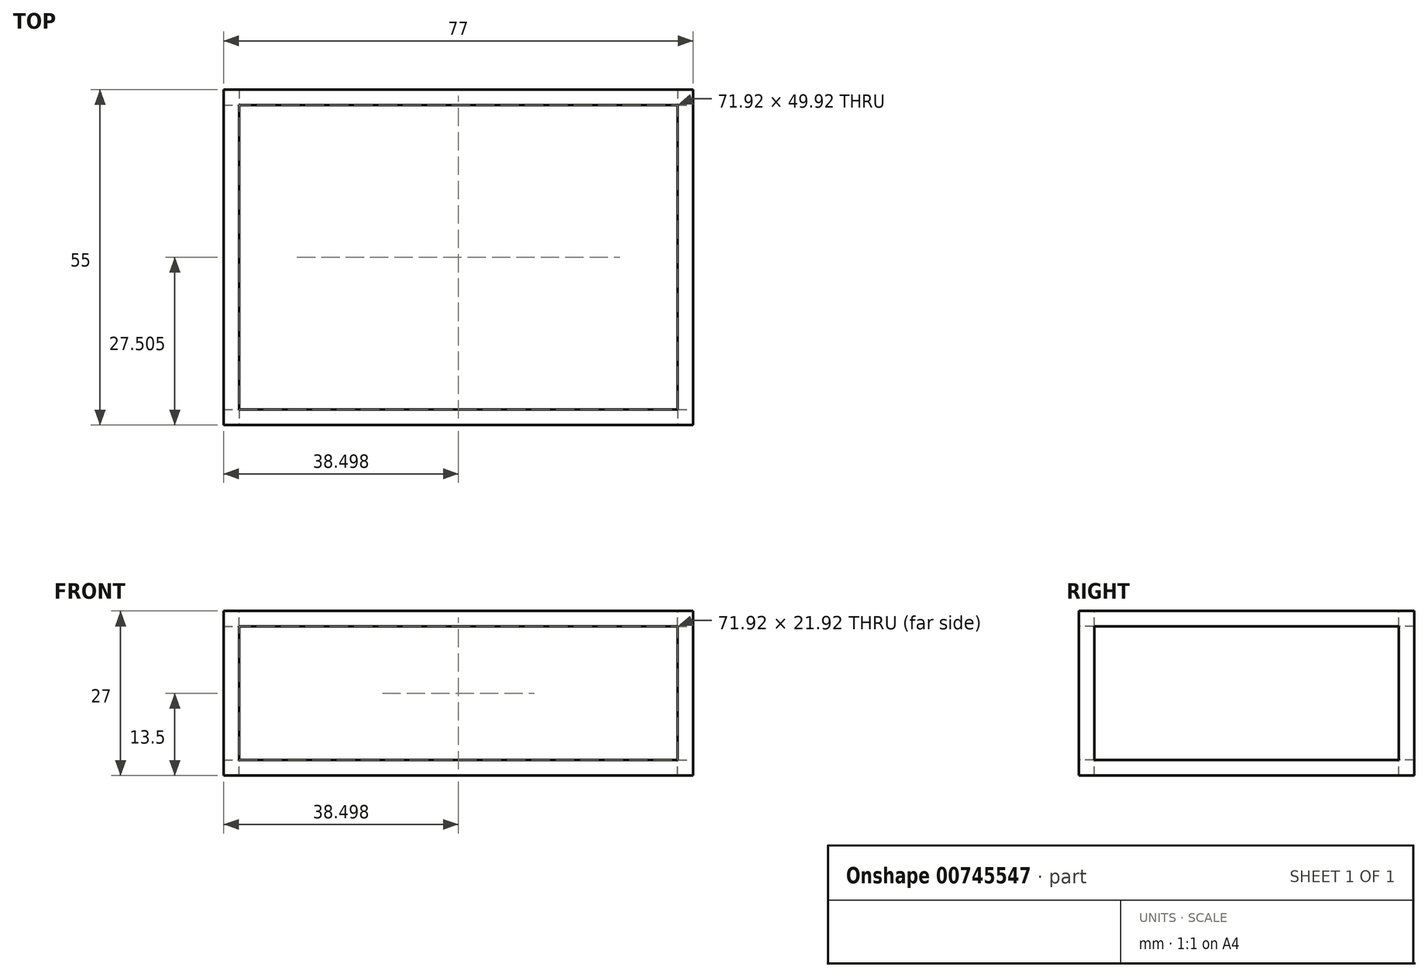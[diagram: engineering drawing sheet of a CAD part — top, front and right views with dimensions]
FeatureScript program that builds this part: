
annotation { "Feature Type Name" : "Feature", "Feature Type Description" : "" }
export const myFeature = defineFeature(function(context is Context, id is Id, definition is map)
    precondition{}
    {
        {
            var Q0;
            Q0=qCreatedBy(makeId("Top.planeOp"),FACE);
            var sketch = newSketch(context, id + "F0", { "sketchPlane" : qUnion([Q0])});
            skLineSegment(sketch, "E0.bottom", {"start": v(-34.82, 42.65) * mm, "end": v(42.18, 42.65) * mm});
            skLineSegment(sketch, "E0.top", {"start": v(-34.82, -12.35) * mm, "end": v(42.18, -12.35) * mm});
            skLineSegment(sketch, "E0.left", {"start": v(-34.82, 42.65) * mm, "end": v(-34.82, -12.35) * mm});
            skLineSegment(sketch, "E0.right", {"start": v(42.18, 42.65) * mm, "end": v(42.18, -12.35) * mm});
            skSolve(sketch);
        }
        {
            var Q0;
            Q0=makeQuery(id+"F0.imprint","IMPRINT",FACE,{"disambiguationData":[TD([[makeQuery(id+"F0.imprint","IMPRINT",EDGE,{"derivedFrom":sQuery(id+"F0.wireOp",EDGE,"E0.bottom")}),-1.0]])]});
            extrude(context, id + "F1", {"entities" : qUnion([Q0]), "depth" : 27 * mm, "offsetDistance" : 25.4 * mm});
        }
        {
            var Q0;
            Q0=makeQuery(id+"F1.opExtrude","CAP_FACE",FACE,{"disambiguationData":[OSD([sQuery(id+"F0.wireOp",EDGE,"E0.bottom"),sQuery(id+"F0.wireOp",EDGE,"E0.top"),sQuery(id+"F0.wireOp",EDGE,"E0.left"),sQuery(id+"F0.wireOp",EDGE,"E0.right")])],"isStart":false});
            var sketch = newSketch(context, id + "F2", { "sketchPlane" : qUnion([Q0])});
            skLineSegment(sketch, "E1.bottom", {"start": v(-32.28, 40.11) * mm, "end": v(39.64, 40.11) * mm});
            skLineSegment(sketch, "E1.top", {"start": v(-32.28, -9.8) * mm, "end": v(39.64, -9.8) * mm});
            skLineSegment(sketch, "E1.left", {"start": v(-32.28, 40.11) * mm, "end": v(-32.28, -9.8) * mm});
            skLineSegment(sketch, "E1.right", {"start": v(39.64, 40.11) * mm, "end": v(39.64, -9.8) * mm});
            skSolve(sketch);
        }
        {
            var Q0;
            Q0=makeQuery(id+"F2.imprint","IMPRINT",FACE,{"disambiguationData":[TD([[makeQuery(id+"F2.imprint","IMPRINT",EDGE,{"derivedFrom":sQuery(id+"F2.wireOp",EDGE,"E1.bottom")}),-1.0]])]});
            extrude(context, id + "F3", {"entities" : qUnion([Q0]), "operationType" : NewBodyOperationType.REMOVE, "oppositeDirection" : true, "depth" : 27 * mm, "offsetDistance" : 25.4 * mm});
        }
        {
            var Q0;
            Q0=makeQuery(id+"F1.opExtrude","SWEPT_FACE",FACE,{"disambiguationData":[OSD([sQuery(id+"F0.wireOp",EDGE,"E0.right")])]});
            var sketch = newSketch(context, id + "F4", { "sketchPlane" : qUnion([Q0])});
            skLineSegment(sketch, "E2.bottom", {"start": v(40.11, 24.46) * mm, "end": v(-9.8, 24.46) * mm});
            skLineSegment(sketch, "E2.top", {"start": v(40.11, 2.54) * mm, "end": v(-9.8, 2.54) * mm});
            skLineSegment(sketch, "E2.left", {"start": v(40.11, 24.46) * mm, "end": v(40.11, 2.54) * mm});
            skLineSegment(sketch, "E2.right", {"start": v(-9.8, 24.46) * mm, "end": v(-9.8, 2.54) * mm});
            skSolve(sketch);
        }
        {
            var Q0;
            Q0=makeQuery(id+"F4.imprint","IMPRINT",FACE,{"disambiguationData":[TD([[makeQuery(id+"F4.imprint","IMPRINT",EDGE,{"derivedFrom":sQuery(id+"F4.wireOp",EDGE,"E2.bottom")}),1.0]])]});
            extrude(context, id + "F5", {"entities" : qUnion([Q0]), "operationType" : NewBodyOperationType.REMOVE, "oppositeDirection" : true, "depth" : 127 * mm, "offsetDistance" : 25.4 * mm});
        }
        {
            var Q0;
            Q0=makeQuery(id+"F1.opExtrude","SWEPT_FACE",FACE,{"disambiguationData":[OSD([sQuery(id+"F0.wireOp",EDGE,"E0.top")])]});
            var sketch = newSketch(context, id + "F6", { "sketchPlane" : qUnion([Q0])});
            skLineSegment(sketch, "E3.bottom", {"start": v(-32.28, 24.46) * mm, "end": v(39.64, 24.46) * mm});
            skLineSegment(sketch, "E3.top", {"start": v(-32.28, 2.54) * mm, "end": v(39.64, 2.54) * mm});
            skLineSegment(sketch, "E3.left", {"start": v(-32.28, 24.46) * mm, "end": v(-32.28, 2.54) * mm});
            skLineSegment(sketch, "E3.right", {"start": v(39.64, 24.46) * mm, "end": v(39.64, 2.54) * mm});
            skSolve(sketch);
        }
        {
            var Q0;
            Q0=makeQuery(id+"F6.imprint","IMPRINT",FACE,{"disambiguationData":[TD([[makeQuery(id+"F6.imprint","IMPRINT",EDGE,{"derivedFrom":sQuery(id+"F6.wireOp",EDGE,"E3.bottom")}),-1.0]])]});
            extrude(context, id + "F7", {"entities" : qUnion([Q0]), "operationType" : NewBodyOperationType.REMOVE, "oppositeDirection" : true, "depth" : 70.1 * mm, "offsetDistance" : 25.4 * mm});
        }
    });
